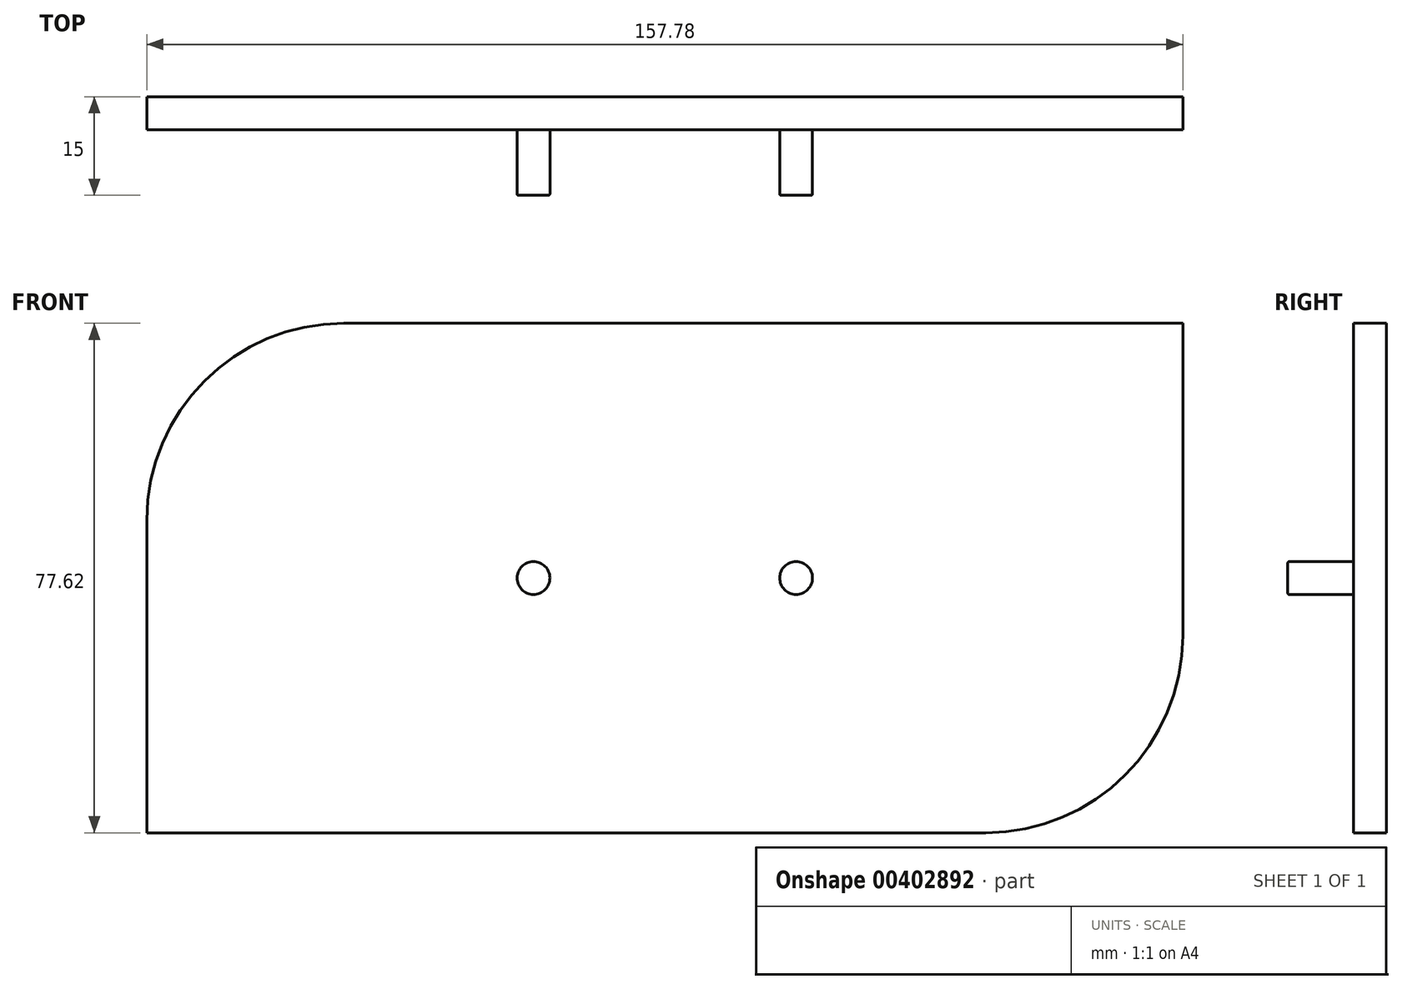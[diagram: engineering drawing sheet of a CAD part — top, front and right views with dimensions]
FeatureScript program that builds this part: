
annotation { "Feature Type Name" : "Feature", "Feature Type Description" : "" }
export const myFeature = defineFeature(function(context is Context, id is Id, definition is map)
    precondition{}
    {
        {
            var Q0;
            Q0=qCreatedBy(makeId("Front.planeOp"),FACE);
            var sketch = newSketch(context, id + "F0", { "sketchPlane" : qUnion([Q0])});
            skLineSegment(sketch, "E0.bottom", {"start": v(78.9, 38.8) * mm, "end": v(-48.9, 38.8) * mm});
            skLineSegment(sketch, "E0.top", {"start": v(48.9, -38.8) * mm, "end": v(-78.9, -38.8) * mm});
            skLineSegment(sketch, "E0.left", {"start": v(78.9, 38.8) * mm, "end": v(78.9, -8.8) * mm});
            skLineSegment(sketch, "E0.right", {"start": v(-78.9, 8.8) * mm, "end": v(-78.9, -38.8) * mm});
            skPoint(sketch, "E0.middle", {"position": v(0, 0) * mm});
            skPoint(sketch, "E1.visualSharp", {"position": v(-78.9, 38.8) * mm});
            skArc(sketch, "E1.filletArc", {"start": v(-48.9, 38.8) * mm, "mid": v(-70.1, 30.02) * mm, "end": v(-78.9, 8.8) * mm});
            skPoint(sketch, "E2.visualSharp", {"position": v(78.9, -38.8) * mm});
            skArc(sketch, "E2.filletArc", {"start": v(48.9, -38.8) * mm, "mid": v(70.1, -30.02) * mm, "end": v(78.9, -8.8) * mm});
            skSolve(sketch);
        }
        {
            var Q0;
            Q0 = qSketchRegion(id + "F0", true);
            extrude(context, id + "F1", {"entities" : qUnion([Q0]), "depth" : 5 * mm});
        }
        {
            var Q0;
            Q0=makeQuery(id+"F1.opExtrude","CAP_FACE",FACE,{"disambiguationData":[OSD([sQuery(id+"F0.wireOp",EDGE,"E0.bottom"),sQuery(id+"F0.wireOp",EDGE,"E0.top"),sQuery(id+"F0.wireOp",EDGE,"E0.left"),sQuery(id+"F0.wireOp",EDGE,"E0.right"),sQuery(id+"F0.wireOp",EDGE,"E1.filletArc"),sQuery(id+"F0.wireOp",EDGE,"E2.filletArc")])],"isStart":false});
            var sketch = newSketch(context, id + "F2", { "sketchPlane" : qUnion([Q0])});
            skCircle(sketch, "E3", {"center": v(-20, 0) * mm, "radius": 2.5 * mm});
            skCircle(sketch, "E4", {"center": v(20, 0) * mm, "radius": 2.5 * mm});
            skSolve(sketch);
        }
        {
            var Q0;
            Q0=makeQuery(id+"F2.imprint","IMPRINT",FACE,{"disambiguationData":[TD([[makeQuery(id+"F2.imprint","IMPRINT",EDGE,{"derivedFrom":sQuery(id+"F2.wireOp",EDGE,"E3")}),1.0]])]});
            var Q1;
            Q1=makeQuery(id+"F2.imprint","IMPRINT",FACE,{"disambiguationData":[TD([[makeQuery(id+"F2.imprint","IMPRINT",EDGE,{"derivedFrom":sQuery(id+"F2.wireOp",EDGE,"E4")}),1.0]])]});
            extrude(context, id + "F3", {"entities" : qUnion([Q0, Q1]), "operationType" : NewBodyOperationType.ADD, "depth" : 10 * mm});
        }
        {
            var Q0;
            Q0=makeQuery(id+"F3.opExtrude","CAP_EDGE",EDGE,{"disambiguationData":[OSD([sQuery(id+"F2.wireOp",EDGE,"E3")])],"isStart":false});
            var Q1;
            Q1=makeQuery(id+"F3.opExtrude","CAP_EDGE",EDGE,{"disambiguationData":[OSD([sQuery(id+"F2.wireOp",EDGE,"E4")])],"isStart":false});
            fillet(context, id + "F4", {"entities" : qUnion([Q0, Q1]), "radius" : .2 * mm, "tangentPropagation" : true, "allowEdgeOverflow" : false});
        }
    });
